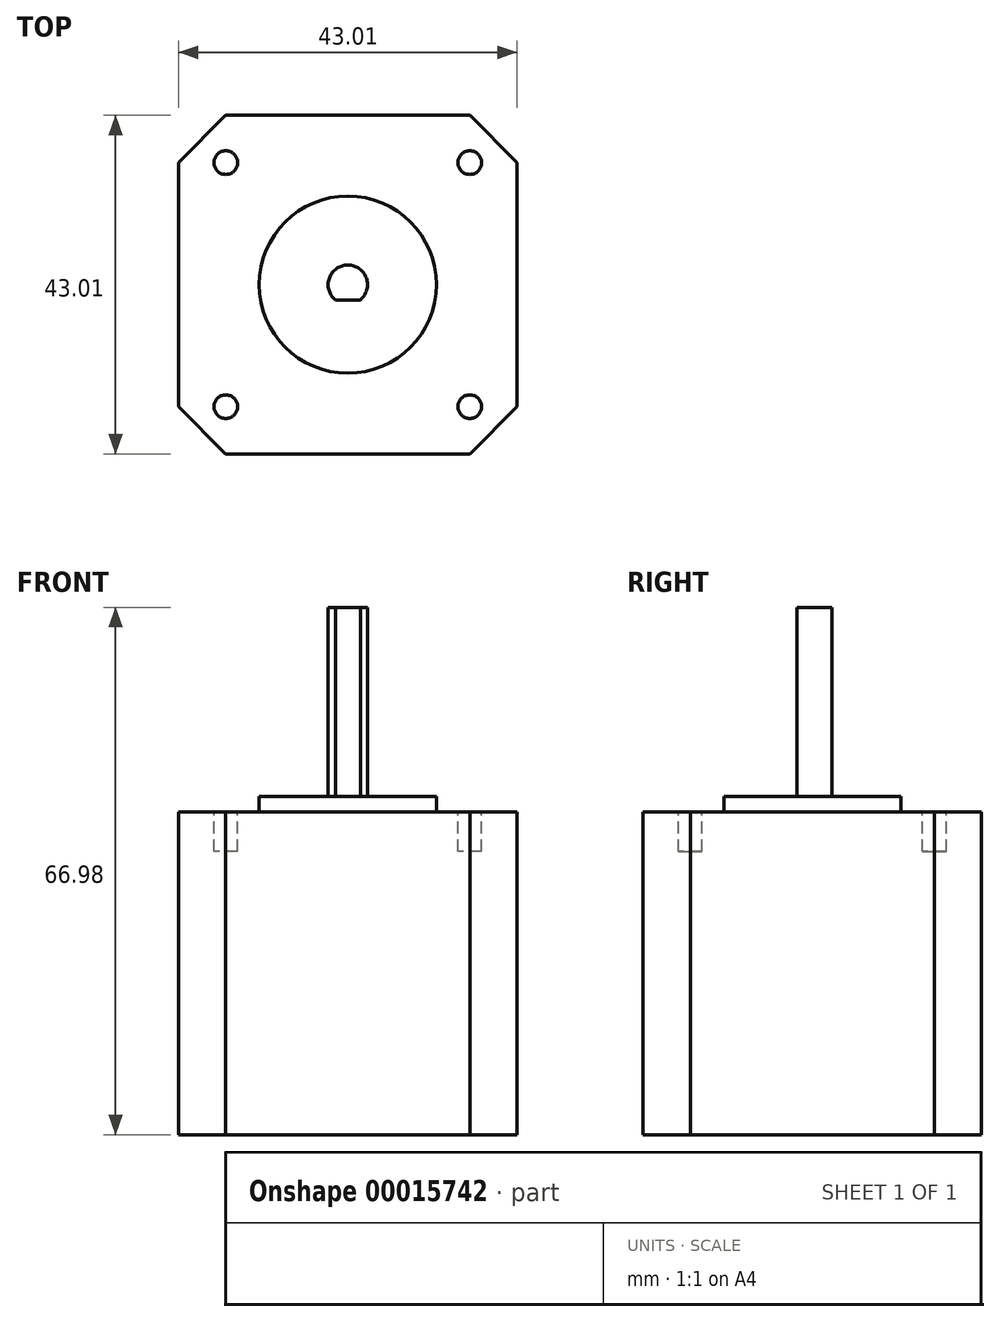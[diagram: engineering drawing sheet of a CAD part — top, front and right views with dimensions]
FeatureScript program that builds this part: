
annotation { "Feature Type Name" : "Feature", "Feature Type Description" : "" }
export const myFeature = defineFeature(function(context is Context, id is Id, definition is map)
    precondition{}
    {
        {
            var Q0;
            Q0=qCreatedBy(makeId("Top.planeOp"),FACE);
            var sketch = newSketch(context, id + "F0", { "sketchPlane" : qUnion([Q0])});
            skLineSegment(sketch, "E0.bottom", {"start": v(0, 0) * mm, "end": v(43, 0) * mm});
            skLineSegment(sketch, "E0.top", {"start": v(0, 43) * mm, "end": v(43, 43) * mm});
            skLineSegment(sketch, "E0.left", {"start": v(0, 0) * mm, "end": v(0, 43) * mm});
            skLineSegment(sketch, "E0.right", {"start": v(43, 0) * mm, "end": v(43, 43) * mm});
            skSolve(sketch);
        }
        {
            var Q0;
            Q0=makeQuery(id+"F0.imprint","IMPRINT",FACE,{"disambiguationData":[TD([[makeQuery(id+"F0.imprint","IMPRINT",EDGE,{"derivedFrom":sQuery(id+"F0.wireOp",EDGE,"E0.bottom")}),1.0]])]});
            extrude(context, id + "F1", {"entities" : qUnion([Q0]), "depth" : 40.98 * mm});
        }
        {
            var Q0;
            Q0=makeQuery(id+"F1.opExtrude","CAP_FACE",FACE,{"disambiguationData":[OSD([sQuery(id+"F0.wireOp",EDGE,"E0.bottom"),sQuery(id+"F0.wireOp",EDGE,"E0.top"),sQuery(id+"F0.wireOp",EDGE,"E0.left"),sQuery(id+"F0.wireOp",EDGE,"E0.right")])],"isStart":false});
            var sketch = newSketch(context, id + "F2", { "sketchPlane" : qUnion([Q0])});
            skLineSegment(sketch, "E1", {"start": v(21.5, 0) * mm, "end": v(21.5, 43) * mm});
            skCircle(sketch, "E2", {"center": v(21.5, 21.5) * mm, "radius": 11.25 * mm});
            skSolve(sketch);
        }
        {
            var Q0;
            Q0=qSketchRegion(id+"F2",true);
            extrude(context, id + "F3", {"entities" : qUnion([Q0]), "operationType" : NewBodyOperationType.ADD, "depth" : 2 * mm});
        }
        {
            var Q0;
            Q0=makeQuery(id+"F1.opExtrude","CAP_FACE",FACE,{"disambiguationData":[OSD([sQuery(id+"F0.wireOp",EDGE,"E0.bottom"),sQuery(id+"F0.wireOp",EDGE,"E0.top"),sQuery(id+"F0.wireOp",EDGE,"E0.left"),sQuery(id+"F0.wireOp",EDGE,"E0.right")])],"isStart":false});
            var sketch = newSketch(context, id + "F4", { "sketchPlane" : qUnion([Q0])});
            skLineSegment(sketch, "E3", {"start": v(6, 21.5) * mm, "end": v(37, 21.5) * mm});
            skLineSegment(sketch, "E4", {"start": v(37, 37) * mm, "end": v(37, 6) * mm});
            skLineSegment(sketch, "E5", {"start": v(6, 37) * mm, "end": v(6, 6) * mm});
            skPoint(sketch, "E6", {"position": v(21.5, 21.5) * mm});
            skCircle(sketch, "E7", {"center": v(6, 6) * mm, "radius": 1.5 * mm});
            skCircle(sketch, "E8", {"center": v(37, 6) * mm, "radius": 1.5 * mm});
            skCircle(sketch, "E9", {"center": v(37, 37) * mm, "radius": 1.5 * mm});
            skCircle(sketch, "E10", {"center": v(6, 37) * mm, "radius": 1.5 * mm});
            skLineSegment(sketch, "E11", {"start": v(21.5, 21.5) * mm, "end": v(21.5, 0) * mm});
            skSolve(sketch);
        }
        {
            var Q0;
            {var subQ0=sQuery(id+"F4.wireOp",EDGE,"E9");var subQ2=sQuery(id+"F4.wireOp",EDGE,"E8");var subQ3=sQuery(id+"F4.wireOp",EDGE,"E10");var subQ5=sQuery(id+"F4.wireOp",EDGE,"E7");Q0=qUnion([makeQuery(id+"F4.imprint","IMPRINT",FACE,{"disambiguationData":[TD([[makeQuery(id+"F4.imprint","IMPRINT",EDGE,{"derivedFrom":subQ0}),1.0]])]}),makeQuery(id+"F4.imprint","IMPRINT",FACE,{"disambiguationData":[TD([[makeQuery(id+"F4.imprint","IMPRINT",EDGE,{"derivedFrom":subQ2}),1.0]])]}),makeQuery(id+"F4.imprint","IMPRINT",FACE,{"disambiguationData":[TD([[makeQuery(id+"F4.imprint","IMPRINT",EDGE,{"derivedFrom":subQ3}),1.0]])]}),makeQuery(id+"F4.imprint","IMPRINT",FACE,{"disambiguationData":[TD([[makeQuery(id+"F4.imprint","IMPRINT",EDGE,{"derivedFrom":subQ5}),1.0]])]})]);}
            extrude(context, id + "F5", {"entities" : qUnion([Q0]), "operationType" : NewBodyOperationType.REMOVE, "oppositeDirection" : true, "depth" : 5 * mm});
        }
        {
            var Q0;
            Q0=makeQuery(id+"F3.opExtrude","CAP_FACE",FACE,{"disambiguationData":[OSD([sQuery(id+"F2.wireOp",EDGE,"E2")])],"isStart":false});
            var sketch = newSketch(context, id + "F6", { "sketchPlane" : qUnion([Q0])});
            skArc(sketch, "E12", {"start": v(23.1, 19.57) * mm, "mid": v(21.5, 24) * mm, "end": v(19.92, 19.57) * mm});
            skLineSegment(sketch, "E13", {"start": v(19.92, 19.57) * mm, "end": v(23.1, 19.57) * mm});
            skLineSegment(sketch, "E14", {"start": v(21.5, 19.57) * mm, "end": v(21.5, 21.5) * mm, "construction": true});
            skSolve(sketch);
        }
        {
            var Q0;
            Q0=qSketchRegion(id+"F6",true);
            extrude(context, id + "F7", {"entities" : qUnion([Q0]), "operationType" : NewBodyOperationType.ADD, "depth" : 24 * mm});
        }
        {
            var Q0;
            Q0=makeQuery(id+"F1.opExtrude","SWEPT_EDGE",EDGE,{"disambiguationData":[OSD([sQuery(id+"F0.wireOp",EDGE,"E0.bottom"),sQuery(id+"F0.wireOp",EDGE,"E0.left")])]});
            var Q1;
            Q1=makeQuery(id+"F1.opExtrude","SWEPT_EDGE",EDGE,{"disambiguationData":[OSD([sQuery(id+"F0.wireOp",EDGE,"E0.top"),sQuery(id+"F0.wireOp",EDGE,"E0.left")])]});
            var Q2;
            Q2=makeQuery(id+"F1.opExtrude","SWEPT_EDGE",EDGE,{"disambiguationData":[OSD([sQuery(id+"F0.wireOp",EDGE,"E0.bottom"),sQuery(id+"F0.wireOp",EDGE,"E0.right")])]});
            var Q3;
            Q3=makeQuery(id+"F1.opExtrude","SWEPT_EDGE",EDGE,{"disambiguationData":[OSD([sQuery(id+"F0.wireOp",EDGE,"E0.top"),sQuery(id+"F0.wireOp",EDGE,"E0.right")])]});
            chamfer(context, id + "F8", {"entities" : qUnion([Q0, Q1, Q2, Q3]), "width" : 6 * mm, "tangentPropagation" : true});
        }
    });
